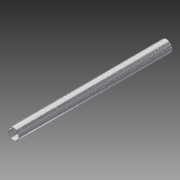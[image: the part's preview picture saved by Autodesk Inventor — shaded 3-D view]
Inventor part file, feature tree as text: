
AUTODESK INVENTOR PART (.ipt)
format: ipt  version: 2013 (Build 170138000, 138)  size: 73,216 bytes
history: native  units: in
note: dims shown in document units (in); Inventor stores cm internally (conversion verified against a paired STEP export)
features: extrude x1, sketch x1
ambient origin geometry x8: Origin, YZ Plane, XZ Plane, XY Plane, X Axis, Y Axis, Z Axis, Center Point
bodies: Solid1 (feature_tree)
feature tree (2):
  extrude  "Extrusion1"  Depth=0.083in
  sketch  "Sketch1"  dims[d0=1.5in d2=0.083in d3=20.0in d4=0.0in]
